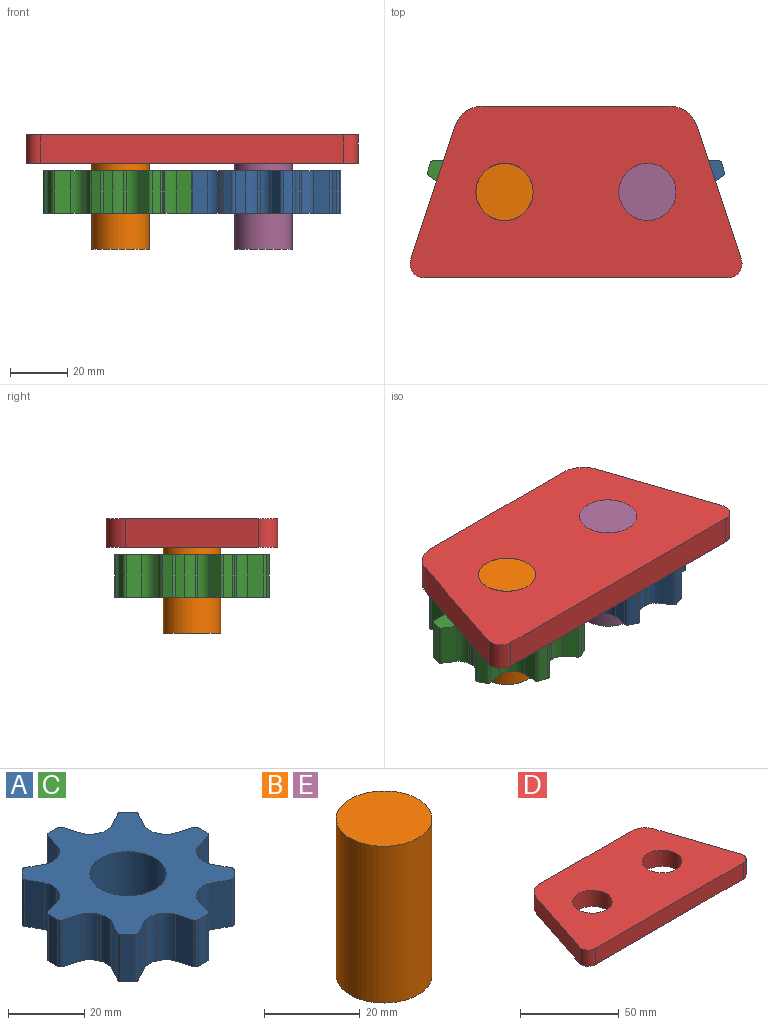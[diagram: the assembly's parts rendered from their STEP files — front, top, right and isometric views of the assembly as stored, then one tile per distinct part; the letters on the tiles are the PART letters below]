
ASSEMBLY  parts=5 mates=4
PART A: 67 faces, bbox 55.6x55.6x15 mm
  f0: plane 15x4.77mm, normal (0.88,-0.48,0), area 81.3mm2, adj f33,f34,f36,f51
  f1: plane 15x2.48mm, normal (0.71,0.71,0), area 52.6mm2, adj f33,f34,f51,f52
  f2: plane 15x4.77mm, normal (-0.48,0.88,0), area 81.3mm2, adj f33,f34,f35,f52
  f3: cylinder r=20mm len=15mm, axis (0,0,-1), area 13.4mm2, adj f33,f34,f35,f38
  f4: plane 15x5.2mm, normal (0.96,0.28,0), area 81.3mm2, adj f33,f34,f38,f53
  f5: plane 15x3.51mm, normal (0,1,0), area 52.6mm2, adj f33,f34,f53,f54
  f6: plane 15x5.2mm, normal (-0.96,0.28,0), area 81.3mm2, adj f33,f34,f37,f54
  f7: cylinder r=20mm len=15mm, axis (0,0,-1), area 13.4mm2, adj f33,f34,f37,f40
  f8: plane 15x4.77mm, normal (0.48,0.88,0), area 81.3mm2, adj f33,f34,f40,f55
  f9: plane 15x2.48mm, normal (-0.71,0.71,0), area 52.6mm2, adj f33,f34,f55,f56
  f10: plane 15x4.77mm, normal (-0.88,-0.48,0), area 81.3mm2, adj f33,f34,f39,f56
  f11: cylinder r=20mm len=15mm, axis (0,0,-1), area 13.4mm2, adj f33,f34,f39,f42
  f12: plane 15x5.2mm, normal (-0.28,0.96,0), area 81.3mm2, adj f33,f34,f42,f57
  f13: plane 15x3.51mm, normal (-1,0,0), area 52.6mm2, adj f33,f34,f57,f58
  f14: plane 15x5.2mm, normal (-0.28,-0.96,0), area 81.3mm2, adj f33,f34,f41,f58
  f15: cylinder r=20mm len=15mm, axis (0,0,-1), area 13.4mm2, adj f33,f34,f41,f44
  f16: plane 15x4.77mm, normal (-0.88,0.48,0), area 81.3mm2, adj f33,f34,f44,f59
  f17: plane 15x2.48mm, normal (-0.71,-0.71,0), area 52.6mm2, adj f33,f34,f59,f60
  f18: plane 15x4.77mm, normal (0.48,-0.88,0), area 81.3mm2, adj f33,f34,f43,f60
  f19: cylinder r=20mm len=15mm, axis (0,0,-1), area 13.4mm2, adj f33,f34,f43,f46
  f20: plane 15x5.2mm, normal (-0.96,-0.28,0), area 81.3mm2, adj f33,f34,f46,f61
  f21: plane 15x3.51mm, normal (0,-1,0), area 52.6mm2, adj f33,f34,f61,f62
  f22: plane 15x5.2mm, normal (0.96,-0.28,0), area 81.3mm2, adj f33,f34,f45,f62
  f23: cylinder r=20mm len=15mm, axis (0,0,-1), area 13.4mm2, adj f33,f34,f45,f48
  f24: plane 15x4.77mm, normal (-0.48,-0.88,0), area 81.3mm2, adj f33,f34,f48,f63
  f25: plane 15x2.48mm, normal (0.71,-0.71,0), area 52.6mm2, adj f33,f34,f63,f64
  f26: plane 15x4.77mm, normal (0.88,0.48,0), area 81.3mm2, adj f33,f34,f47,f64
  f27: cylinder r=20mm len=15mm, axis (0,0,-1), area 13.4mm2, adj f33,f34,f47,f50
  f28: plane 15x5.2mm, normal (0.28,-0.96,0), area 81.3mm2, adj f33,f34,f50,f66
  f29: plane 15x3.51mm, normal (1,0,0), area 52.6mm2, adj f33,f34,f65,f66
  f30: plane 15x5.2mm, normal (0.28,0.96,0), area 81.3mm2, adj f33,f34,f49,f65
  f31: cylinder r=20mm len=15mm, axis (0,0,-1), area 13.4mm2, adj f33,f34,f36,f49
  f32: cylinder r=10mm len=20mm, axis (0,0,-1), area 942.5mm2, adj f33,f34
  f33: plane 55.6x55.6mm, normal (0,0,1), area 1428.6mm2, adj f0,f1,f2,f3,f4,f5,f6,f7
  f34: plane 55.6x55.6mm, normal (0,0,-1), area 1428.6mm2, adj f0,f1,f2,f3,f4,f5,f6,f7
  f35: cylinder r=5mm len=15mm, axis (0,0,-1), area 68.4mm2, adj f2,f3,f33,f34
  f36: cylinder r=5mm len=15mm, axis (0,0,-1), area 68.4mm2, adj f0,f31,f33,f34
  f37: cylinder r=5mm len=15mm, axis (0,0,-1), area 68.4mm2, adj f6,f7,f33,f34
  f38: cylinder r=5mm len=15mm, axis (0,0,-1), area 68.4mm2, adj f3,f4,f33,f34
  f39: cylinder r=5mm len=15mm, axis (0,0,-1), area 68.4mm2, adj f10,f11,f33,f34
  f40: cylinder r=5mm len=15mm, axis (0,0,-1), area 68.4mm2, adj f7,f8,f33,f34
  f41: cylinder r=5mm len=15mm, axis (0,0,-1), area 68.4mm2, adj f14,f15,f33,f34
  f42: cylinder r=5mm len=15mm, axis (0,0,-1), area 68.4mm2, adj f11,f12,f33,f34
  f43: cylinder r=5mm len=15mm, axis (0,0,-1), area 68.4mm2, adj f18,f19,f33,f34
  f44: cylinder r=5mm len=15mm, axis (0,0,-1), area 68.4mm2, adj f15,f16,f33,f34
  f45: cylinder r=5mm len=15mm, axis (0,0,-1), area 68.4mm2, adj f22,f23,f33,f34
  f46: cylinder r=5mm len=15mm, axis (0,0,-1), area 68.4mm2, adj f19,f20,f33,f34
  f47: cylinder r=5mm len=15mm, axis (0,0,-1), area 68.4mm2, adj f26,f27,f33,f34
  f48: cylinder r=5mm len=15mm, axis (0,0,-1), area 68.4mm2, adj f23,f24,f33,f34
  f49: cylinder r=5mm len=15mm, axis (0,0,-1), area 68.4mm2, adj f30,f31,f33,f34
  f50: cylinder r=5mm len=15mm, axis (0,0,-1), area 68.4mm2, adj f27,f28,f33,f34
  f51: cylinder r=1mm len=15mm, axis (0,0,-1), area 19.2mm2, adj f0,f1,f33,f34
  f52: cylinder r=1mm len=15mm, axis (0,0,1), area 19.2mm2, adj f1,f2,f33,f34
  f53: cylinder r=1mm len=15mm, axis (0,0,-1), area 19.2mm2, adj f4,f5,f33,f34
  f54: cylinder r=1mm len=15mm, axis (0,0,1), area 19.2mm2, adj f5,f6,f33,f34
  f55: cylinder r=1mm len=15mm, axis (0,0,-1), area 19.2mm2, adj f8,f9,f33,f34
  f56: cylinder r=1mm len=15mm, axis (0,0,1), area 19.2mm2, adj f9,f10,f33,f34
  f57: cylinder r=1mm len=15mm, axis (0,0,-1), area 19.2mm2, adj f12,f13,f33,f34
  f58: cylinder r=1mm len=15mm, axis (0,0,1), area 19.2mm2, adj f13,f14,f33,f34
  f59: cylinder r=1mm len=15mm, axis (0,0,-1), area 19.2mm2, adj f16,f17,f33,f34
  f60: cylinder r=1mm len=15mm, axis (0,0,1), area 19.2mm2, adj f17,f18,f33,f34
  f61: cylinder r=1mm len=15mm, axis (0,0,-1), area 19.2mm2, adj f20,f21,f33,f34
  f62: cylinder r=1mm len=15mm, axis (0,0,1), area 19.2mm2, adj f21,f22,f33,f34
  f63: cylinder r=1mm len=15mm, axis (0,0,-1), area 19.2mm2, adj f24,f25,f33,f34
  f64: cylinder r=1mm len=15mm, axis (0,0,1), area 19.2mm2, adj f25,f26,f33,f34
  f65: cylinder r=1mm len=15mm, axis (0,0,-1), area 19.2mm2, adj f29,f30,f33,f34
  f66: cylinder r=1mm len=15mm, axis (0,0,1), area 19.2mm2, adj f28,f29,f33,f34
PART B: 3 faces, bbox 20x20x40 mm
  f0: cylinder r=10mm len=40mm, axis (0,0,-1), area 2513.3mm2, adj f1,f2
  f1: plane 20x20mm, normal (0,0,1), area 314.2mm2, adj f0
  f2: plane 20x20mm, normal (0,0,-1), area 314.2mm2, adj f0
PART C: same geometry as A
PART D: 12 faces, bbox 116.1x60x10 mm
  f0: plane 106.13x10mm, normal (0,-1,0), area 1061.3mm2, adj f1,f9,f10,f11
  f1: cylinder r=5mm len=10mm, axis (0,0,-1), area 94.6mm2, adj f0,f2,f10,f11
  f2: plane 46.58x15.53mm, normal (0.95,0.32,0), area 491mm2, adj f1,f3,f10,f11
  f3: cylinder r=10mm len=10mm, axis (0,0,-1), area 124.9mm2, adj f2,f4,f10,f11
  f4: plane 65.59x10mm, normal (0,1,0), area 655.8mm2, adj f3,f5,f10,f11
  f5: cylinder r=10mm len=10mm, axis (0,0,-1), area 124.9mm2, adj f4,f6,f10,f11
  f6: plane 46.58x15.53mm, normal (-0.95,0.32,0), area 491mm2, adj f5,f9,f10,f11
  f7: cylinder r=10mm len=20mm, axis (0,0,-1), area 628.3mm2, adj f10,f11
  f8: cylinder r=10mm len=20mm, axis (0,0,-1), area 628.3mm2, adj f10,f11
  f9: cylinder r=5mm len=10mm, axis (0,0,-1), area 94.6mm2, adj f0,f6,f10,f11
  f10: plane 116.13x60mm, normal (0,0,1), area 5330.4mm2, adj f0,f1,f2,f3,f4,f5,f6,f7
  f11: plane 116.13x60mm, normal (0,0,-1), area 5330.4mm2, adj f0,f1,f2,f3,f4,f5,f6,f7
PART E: same geometry as B
PLACE A rot(axis=(0,0,1),63.1deg) t=(117.55,26.04,36.64)mm
PLACE B rot(axis=(0,0,1),180deg) t=(17.82,57.69,24.14)mm
PLACE C rot(axis=(0,0,1),116.9deg) t=(67.55,26.04,36.64)mm
PLACE D t=(-7.19,70.88,54.14)mm fixed
PLACE E t=(167.29,-5.62,24.14)mm
MATE revolute C.f32 <-> B.f0  axis (0,0,-1) through (67.55,26.04,44.14)mm
MATE fastened B.f0 <-> D.f7  axis (0,0,-1) through (67.55,26.04,64.14)mm
MATE fastened E.f0 <-> D.f8  axis (0,0,-1) through (117.55,26.04,64.14)mm
MATE revolute A.f32 <-> E.f0  axis (0,0,-1) through (117.55,26.04,44.14)mm
